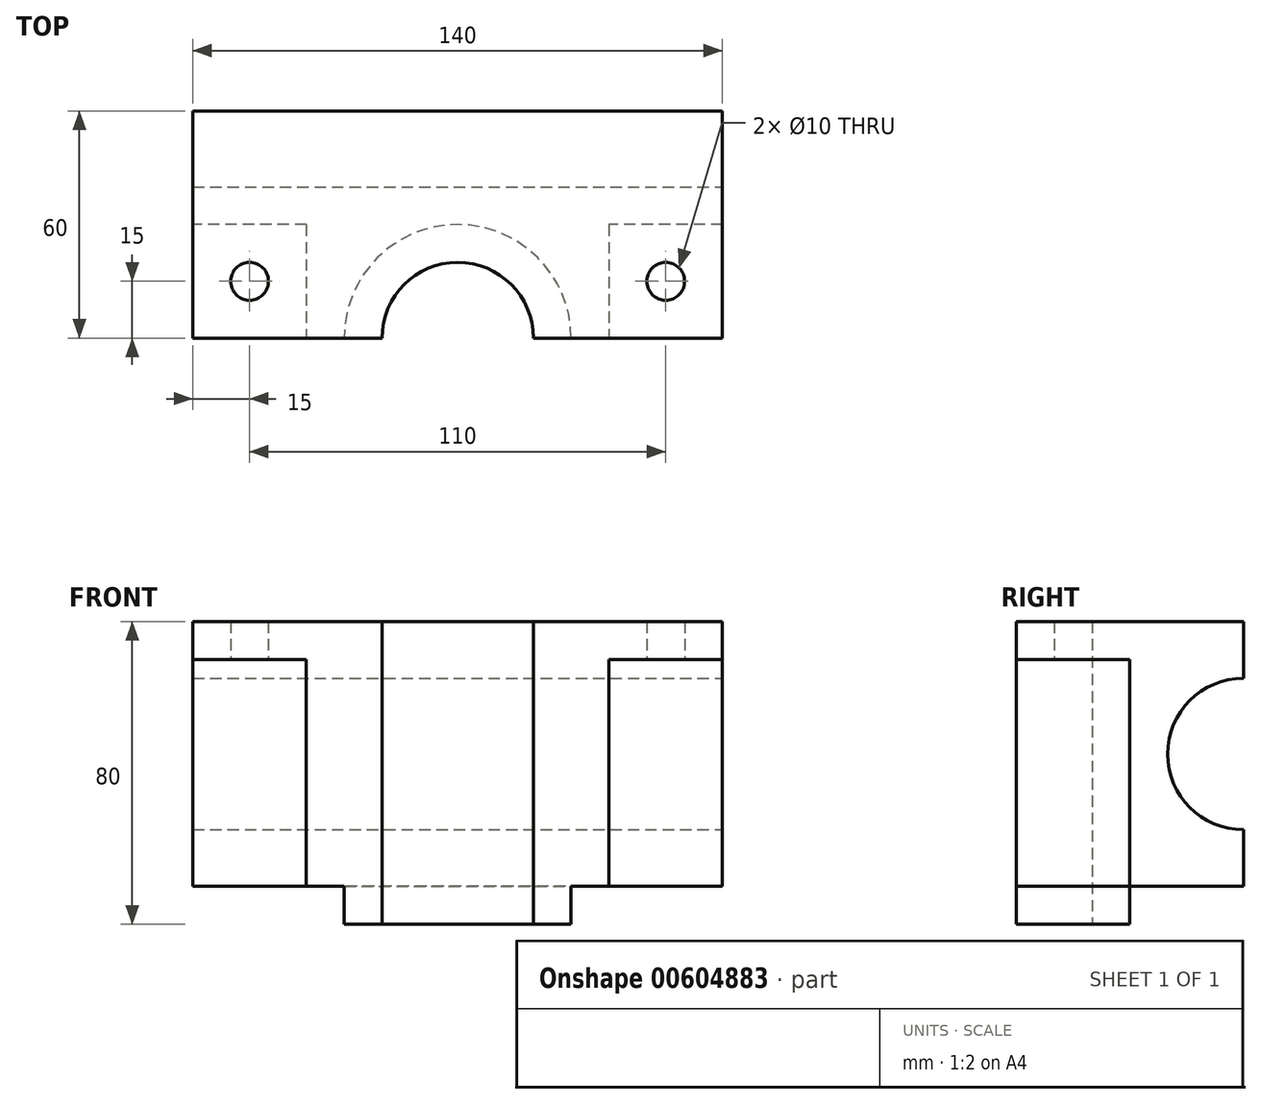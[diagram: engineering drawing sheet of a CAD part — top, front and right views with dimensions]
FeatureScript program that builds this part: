
annotation { "Feature Type Name" : "Feature", "Feature Type Description" : "" }
export const myFeature = defineFeature(function(context is Context, id is Id, definition is map)
    precondition{}
    {
        {
            var Q0;
            Q0=qCreatedBy(makeId("Front.planeOp"),FACE);
            var sketch = newSketch(context, id + "F0", { "sketchPlane" : qUnion([Q0])});
            skLineSegment(sketch, "E0.bottom", {"start": v(70, -35) * mm, "end": v(-70, -35) * mm});
            skLineSegment(sketch, "E0.top", {"start": v(70, 35) * mm, "end": v(-70, 35) * mm});
            skLineSegment(sketch, "E0.left", {"start": v(70, -35) * mm, "end": v(70, 35) * mm});
            skLineSegment(sketch, "E0.right", {"start": v(-70, -35) * mm, "end": v(-70, 35) * mm});
            skPoint(sketch, "E0.middle", {"position": v(0, 0) * mm});
            skSolve(sketch);
        }
        {
            var Q0;
            Q0=makeQuery(id+"F0.imprint","IMPRINT",FACE,{"disambiguationData":[TD([[makeQuery(id+"F0.imprint","IMPRINT",EDGE,{"derivedFrom":sQuery(id+"F0.wireOp",EDGE,"E0.bottom")}),-1.0]])]});
            extrude(context, id + "F1", {"entities" : qUnion([Q0]), "depth" : 60 * mm, "offsetDistance" : 25 * mm});
        }
        {
            var Q0;
            Q0=makeQuery(id+"F1.opExtrude","CAP_FACE",FACE,{"disambiguationData":[OSD([sQuery(id+"F0.wireOp",EDGE,"E0.bottom"),sQuery(id+"F0.wireOp",EDGE,"E0.top"),sQuery(id+"F0.wireOp",EDGE,"E0.left"),sQuery(id+"F0.wireOp",EDGE,"E0.right")])],"isStart":false});
            var sketch = newSketch(context, id + "F2", { "sketchPlane" : qUnion([Q0])});
            skLineSegment(sketch, "E1.bottom", {"start": v(70, -35) * mm, "end": v(40, -35) * mm});
            skLineSegment(sketch, "E1.top", {"start": v(70, 25) * mm, "end": v(40, 25) * mm});
            skLineSegment(sketch, "E1.left", {"start": v(70, -35) * mm, "end": v(70, 25) * mm});
            skLineSegment(sketch, "E1.right", {"start": v(40, -35) * mm, "end": v(40, 25) * mm});
            skSolve(sketch);
        }
        {
            var Q0;
            Q0=makeQuery(id+"F2.imprint","IMPRINT",FACE,{"disambiguationData":[TD([[makeQuery(id+"F2.imprint","IMPRINT",EDGE,{"derivedFrom":sQuery(id+"F2.wireOp",EDGE,"E1.bottom")}),-1.0]])]});
            extrude(context, id + "F3", {"entities" : qUnion([Q0]), "operationType" : NewBodyOperationType.REMOVE, "oppositeDirection" : true, "depth" : 30 * mm, "offsetDistance" : 25 * mm});
        }
        {
            var Q0;
            Q0=makeQuery(id+"F1.opExtrude","CAP_FACE",FACE,{"disambiguationData":[OSD([sQuery(id+"F0.wireOp",EDGE,"E0.bottom"),sQuery(id+"F0.wireOp",EDGE,"E0.top"),sQuery(id+"F0.wireOp",EDGE,"E0.left"),sQuery(id+"F0.wireOp",EDGE,"E0.right")])],"isStart":false});
            var sketch = newSketch(context, id + "F4", { "sketchPlane" : qUnion([Q0])});
            skLineSegment(sketch, "E2.bottom", {"start": v(-70, -35) * mm, "end": v(-40, -35) * mm});
            skLineSegment(sketch, "E2.top", {"start": v(-70, 25) * mm, "end": v(-40, 25) * mm});
            skLineSegment(sketch, "E2.left", {"start": v(-70, -35) * mm, "end": v(-70, 25) * mm});
            skLineSegment(sketch, "E2.right", {"start": v(-40, -35) * mm, "end": v(-40, 25) * mm});
            skSolve(sketch);
        }
        {
            var Q0;
            Q0=makeQuery(id+"F4.imprint","IMPRINT",FACE,{"disambiguationData":[TD([[makeQuery(id+"F4.imprint","IMPRINT",EDGE,{"derivedFrom":sQuery(id+"F4.wireOp",EDGE,"E2.bottom")}),-1.0]])]});
            extrude(context, id + "F5", {"entities" : qUnion([Q0]), "operationType" : NewBodyOperationType.REMOVE, "oppositeDirection" : true, "depth" : 30 * mm, "offsetDistance" : 25 * mm});
        }
        {
            var Q0;
            Q0=makeQuery(id+"F1.opExtrude","SWEPT_FACE",FACE,{"disambiguationData":[OSD([sQuery(id+"F0.wireOp",EDGE,"E0.left")])]});
            var sketch = newSketch(context, id + "F6", { "sketchPlane" : qUnion([Q0])});
            skCircle(sketch, "E3", {"center": v(0, 0) * mm, "radius": 20 * mm});
            skSolve(sketch);
        }
        {
            var Q0;
            {var subQ0=sQuery(id+"F6.wireOp",EDGE,"E3");var subQ1=makeQuery(id+"F1.opExtrude","CAP_EDGE",EDGE,{"disambiguationData":[OSD([sQuery(id+"F0.wireOp",EDGE,"E0.left")])],"isStart":true});var subQ2=makeQuery(id+"F6.imprint","INTERSECT",VERTEX,{"disambiguationData":[OD(0.0)],"derivedFrom":[subQ1,subQ0]});Q0=makeQuery(id+"F6.imprint","IMPRINT",FACE,{"disambiguationData":[TD([[makeQuery(id+"F6.imprint","IMPRINT",EDGE,{"disambiguationData":[TD([[subQ2,1.0]])],"derivedFrom":subQ0}),1.0]])]});}
            extrude(context, id + "F7", {"entities" : qUnion([Q0]), "operationType" : NewBodyOperationType.REMOVE, "oppositeDirection" : true, "depth" : 148 * mm, "offsetDistance" : 25 * mm});
        }
        {
            var Q0;
            Q0=makeQuery(id+"F1.opExtrude","SWEPT_FACE",FACE,{"disambiguationData":[OSD([sQuery(id+"F0.wireOp",EDGE,"E0.bottom")])]});
            var sketch = newSketch(context, id + "F8", { "sketchPlane" : qUnion([Q0])});
            skCircle(sketch, "E4", {"center": v(0, 60) * mm, "radius": 20 * mm});
            skCircle(sketch, "E5", {"center": v(0, 60) * mm, "radius": 30 * mm});
            skSolve(sketch);
        }
        {
            var Q0;
            {var subQ0=sQuery(id+"F8.wireOp",EDGE,"E4");var subQ1=makeQuery(id+"F1.opExtrude","CAP_EDGE",EDGE,{"disambiguationData":[OSD([sQuery(id+"F0.wireOp",EDGE,"E0.bottom")])],"isStart":false});var subQ2=makeQuery(id+"F8.imprint","INTERSECT",VERTEX,{"disambiguationData":[OD(0.0)],"derivedFrom":[subQ1,subQ0]});Q0=makeQuery(id+"F8.imprint","IMPRINT",FACE,{"disambiguationData":[TD([[makeQuery(id+"F8.imprint","IMPRINT",EDGE,{"disambiguationData":[TD([[subQ2,1.0]])],"derivedFrom":subQ0}),1.0]])]});}
            extrude(context, id + "F9", {"entities" : qUnion([Q0]), "operationType" : NewBodyOperationType.REMOVE, "oppositeDirection" : true, "depth" : 269.3 * mm, "offsetDistance" : 25 * mm});
        }
        {
            var Q0;
            {var subQ0=sQuery(id+"F8.wireOp",EDGE,"E4");var subQ1=makeQuery(id+"F1.opExtrude","CAP_EDGE",EDGE,{"disambiguationData":[OSD([sQuery(id+"F0.wireOp",EDGE,"E0.bottom")])],"isStart":false});var subQ2=makeQuery(id+"F8.imprint","INTERSECT",VERTEX,{"disambiguationData":[OD(0.0)],"derivedFrom":[subQ1,subQ0]});Q0=makeQuery(id+"F8.imprint","IMPRINT",FACE,{"disambiguationData":[TD([[makeQuery(id+"F8.imprint","IMPRINT",EDGE,{"disambiguationData":[TD([[subQ2,1.0]])],"derivedFrom":subQ0}),-1.0]])]});}
            extrude(context, id + "F10", {"entities" : qUnion([Q0]), "operationType" : NewBodyOperationType.ADD, "depth" : 10 * mm, "offsetDistance" : 25 * mm});
        }
        {
            var Q0;
            Q0=makeQuery(id+"F3.boolean.opBoolean","COPY",FACE,{"derivedFrom":makeQuery(id+"F3.opExtrude","SWEPT_FACE",FACE,{"disambiguationData":[OSD([sQuery(id+"F2.wireOp",EDGE,"E1.top")])]})});
            var sketch = newSketch(context, id + "F11", { "sketchPlane" : qUnion([Q0])});
            skCircle(sketch, "E6", {"center": v(55, 45) * mm, "radius": 5 * mm});
            skCircle(sketch, "E7.MirrorC", {"center": v(-55, 45) * mm, "radius": 5 * mm});
            skSolve(sketch);
        }
        {
            var Q0;
            Q0=makeQuery(id+"F11.imprint","IMPRINT",FACE,{"disambiguationData":[TD([[makeQuery(id+"F11.imprint","IMPRINT",EDGE,{"derivedFrom":sQuery(id+"F11.wireOp",EDGE,"E6")}),1.0]])]});
            extrude(context, id + "F12", {"entities" : qUnion([Q0]), "operationType" : NewBodyOperationType.REMOVE, "oppositeDirection" : true, "depth" : 25 * mm, "offsetDistance" : 25 * mm});
        }
        {
            var Q0;
            Q0 = qSketchRegion(id + "F11", true);
            extrude(context, id + "F13", {"entities" : qUnion([Q0]), "operationType" : NewBodyOperationType.REMOVE, "oppositeDirection" : true, "depth" : 25 * mm, "offsetDistance" : 25 * mm});
        }
    });
